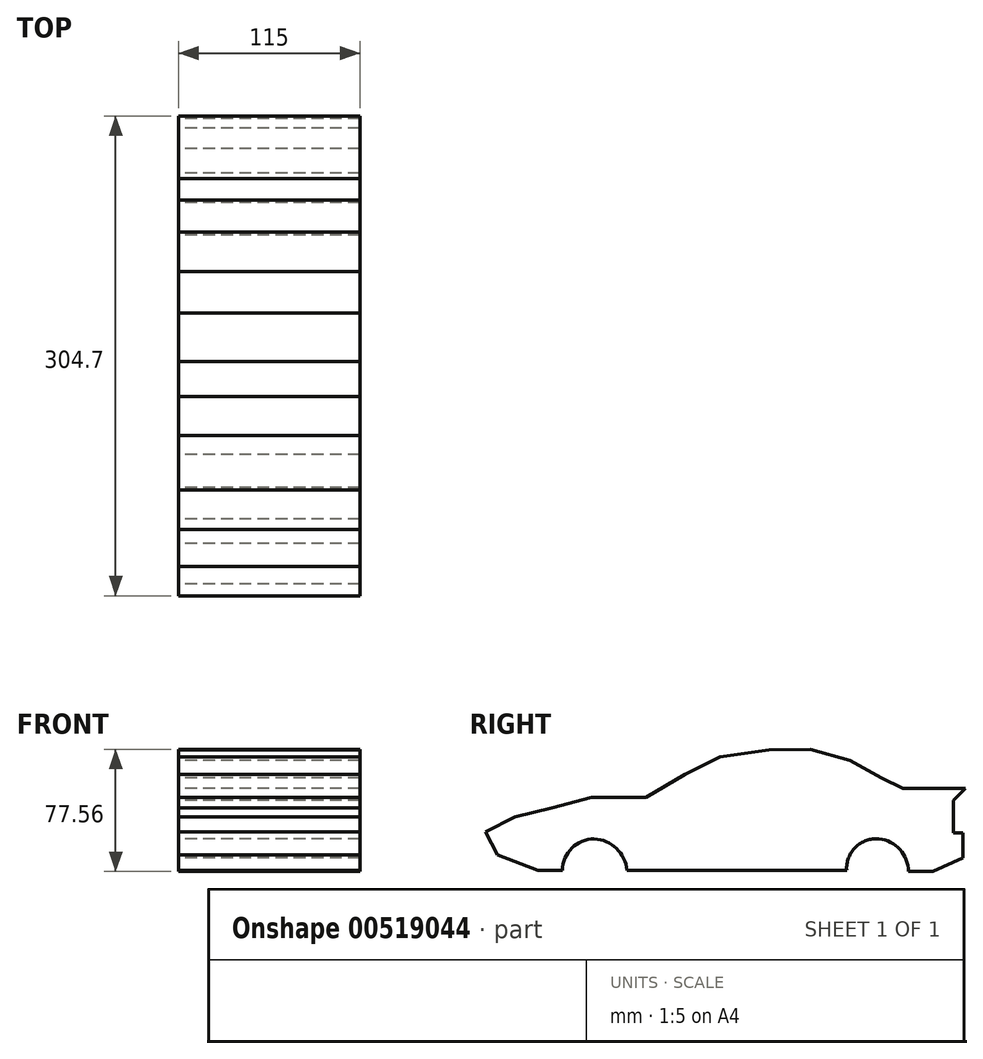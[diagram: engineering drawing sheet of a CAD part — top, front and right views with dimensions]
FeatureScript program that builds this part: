
annotation { "Feature Type Name" : "Feature", "Feature Type Description" : "" }
export const myFeature = defineFeature(function(context is Context, id is Id, definition is map)
    precondition{}
    {
        {
            var Q0;
            Q0=qCreatedBy(makeId("Right.planeOp"),FACE);
            var sketch = newSketch(context, id + "F0", { "sketchPlane" : qUnion([Q0])});
            skLineSegment(sketch, "E0", {"start": v(-114.75, 0) * mm, "end": v(-89.64, 6.74) * mm});
            skLineSegment(sketch, "E1", {"start": v(-89.64, 6.74) * mm, "end": v(-55.13, 6.74) * mm});
            skLineSegment(sketch, "E2", {"start": v(-55.13, 6.74) * mm, "end": v(-30.22, 21.24) * mm});
            skLineSegment(sketch, "E3", {"start": v(-30.22, 21.24) * mm, "end": v(-7.96, 32.47) * mm});
            skLineSegment(sketch, "E4", {"start": v(-7.96, 32.47) * mm, "end": v(22.87, 36.75) * mm});
            skLineSegment(sketch, "E5", {"start": v(22.87, 36.75) * mm, "end": v(49.2, 37.16) * mm});
            skLineSegment(sketch, "E6", {"start": v(49.2, 37.16) * mm, "end": v(74.33, 30.02) * mm});
            skLineSegment(sketch, "E7", {"start": v(74.33, 30.02) * mm, "end": v(94.54, 18.99) * mm});
            skLineSegment(sketch, "E8", {"start": v(94.54, 18.99) * mm, "end": v(108.22, 12.25) * mm});
            skLineSegment(sketch, "E9", {"start": v(108.22, 12.25) * mm, "end": v(140.07, 12.25) * mm});
            skLineSegment(sketch, "E10", {"start": v(140.07, 12.25) * mm, "end": v(147.83, 12.25) * mm});
            skLineSegment(sketch, "E11", {"start": v(147.83, 12.25) * mm, "end": v(140.07, 4.84) * mm});
            skLineSegment(sketch, "E12", {"start": v(140.07, 4.84) * mm, "end": v(140.07, -15.82) * mm});
            skLineSegment(sketch, "E13", {"start": v(140.07, -15.82) * mm, "end": v(146.11, -15.82) * mm});
            skLineSegment(sketch, "E14", {"start": v(146.11, -15.82) * mm, "end": v(146.11, -31.88) * mm});
            skLineSegment(sketch, "E15", {"start": v(146.11, -31.88) * mm, "end": v(127.21, -40.4) * mm});
            skLineSegment(sketch, "E16", {"start": v(127.21, -40.4) * mm, "end": v(111.6, -40.4) * mm});
            skArc(sketch, "E17", {"start": v(111.6, -40.4) * mm, "mid": v(106.2, -26.5) * mm, "end": v(92.9, -19.76) * mm});
            skArc(sketch, "E18", {"start": v(92.9, -19.76) * mm, "mid": v(78.03, -25.04) * mm, "end": v(72.38, -39.76) * mm});
            skLineSegment(sketch, "E19", {"start": v(72.38, -39.76) * mm, "end": v(-37.21, -39.76) * mm});
            skLineSegment(sketch, "E20", {"start": v(-114.75, 0) * mm, "end": v(-138.2, -5.88) * mm});
            skLineSegment(sketch, "E21", {"start": v(-138.2, -5.88) * mm, "end": v(-156.87, -15.22) * mm});
            skLineSegment(sketch, "E22", {"start": v(-156.87, -15.22) * mm, "end": v(-149.5, -29.95) * mm});
            skLineSegment(sketch, "E23", {"start": v(-149.5, -29.95) * mm, "end": v(-123.76, -39.76) * mm});
            skLineSegment(sketch, "E24", {"start": v(-123.76, -39.76) * mm, "end": v(-108.14, -39.76) * mm});
            skLineSegment(sketch, "E25", {"start": v(-37.21, -39.76) * mm, "end": v(-67.2, -39.76) * mm});
            skArc(sketch, "E26", {"start": v(-88, -19.76) * mm, "mid": v(-102.2, -25.6) * mm, "end": v(-108.14, -39.76) * mm});
            skArc(sketch, "E27", {"start": v(-67.2, -39.76) * mm, "mid": v(-73.83, -25.85) * mm, "end": v(-88, -19.76) * mm});
            skSolve(sketch);
        }
        {
            var Q0;
            Q0 = qSketchRegion(id + "F0", true);
            extrude(context, id + "F1", {"entities" : qUnion([Q0]), "depth" : 115 * mm, "offsetDistance" : 25 * mm});
        }
    });
